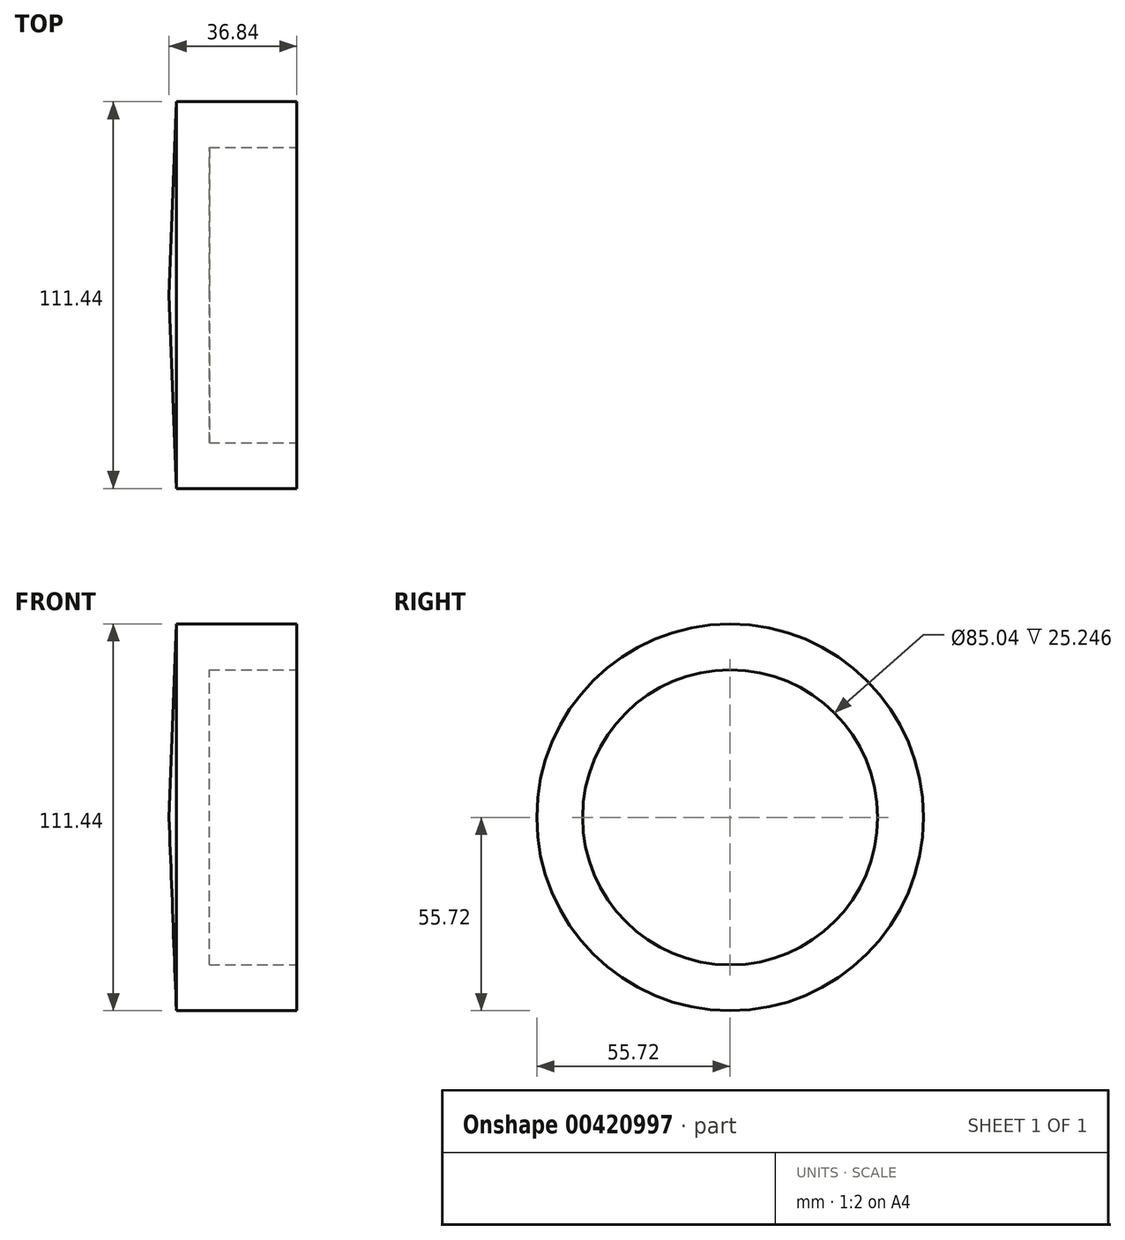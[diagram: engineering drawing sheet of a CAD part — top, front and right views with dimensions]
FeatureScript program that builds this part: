
annotation { "Feature Type Name" : "Feature", "Feature Type Description" : "" }
export const myFeature = defineFeature(function(context is Context, id is Id, definition is map)
    precondition{}
    {
        {
            var Q0;
            Q0=qCreatedBy(makeId("Front.planeOp"),FACE);
            var sketch = newSketch(context, id + "F0", { "sketchPlane" : qUnion([Q0])});
            skLineSegment(sketch, "E0", {"start": v(2.13, 55.72) * mm, "end": v(36.84, 55.72) * mm});
            skLineSegment(sketch, "E1", {"start": v(36.84, 55.72) * mm, "end": v(36.84, 42.52) * mm});
            skLineSegment(sketch, "E2", {"start": v(36.84, 42.52) * mm, "end": v(11.6, 42.52) * mm});
            skLineSegment(sketch, "E3", {"start": v(11.6, 42.52) * mm, "end": v(11.6, 0) * mm});
            skLineSegment(sketch, "E4", {"start": v(11.6, 0) * mm, "end": v(0, 0) * mm});
            skLineSegment(sketch, "E5", {"start": v(0, 0) * mm, "end": v(2.13, 55.72) * mm});
            skSolve(sketch);
        }
        {
            var Q0;
            Q0=makeQuery(id+"F0.imprint","IMPRINT",FACE,{"disambiguationData":[TD([[makeQuery(id+"F0.imprint","IMPRINT",EDGE,{"derivedFrom":sQuery(id+"F0.wireOp",EDGE,"E0")}),-1.0]])]});
            var Q1;
            Q1=sQuery(id+"F0.wireOp",EDGE,"E4");
            revolve(context, id + "F1", {"entities" : qUnion([Q0]), "axis" : qUnion([Q1]), "revolveType" : RevolveType.FULL});
        }
    });
